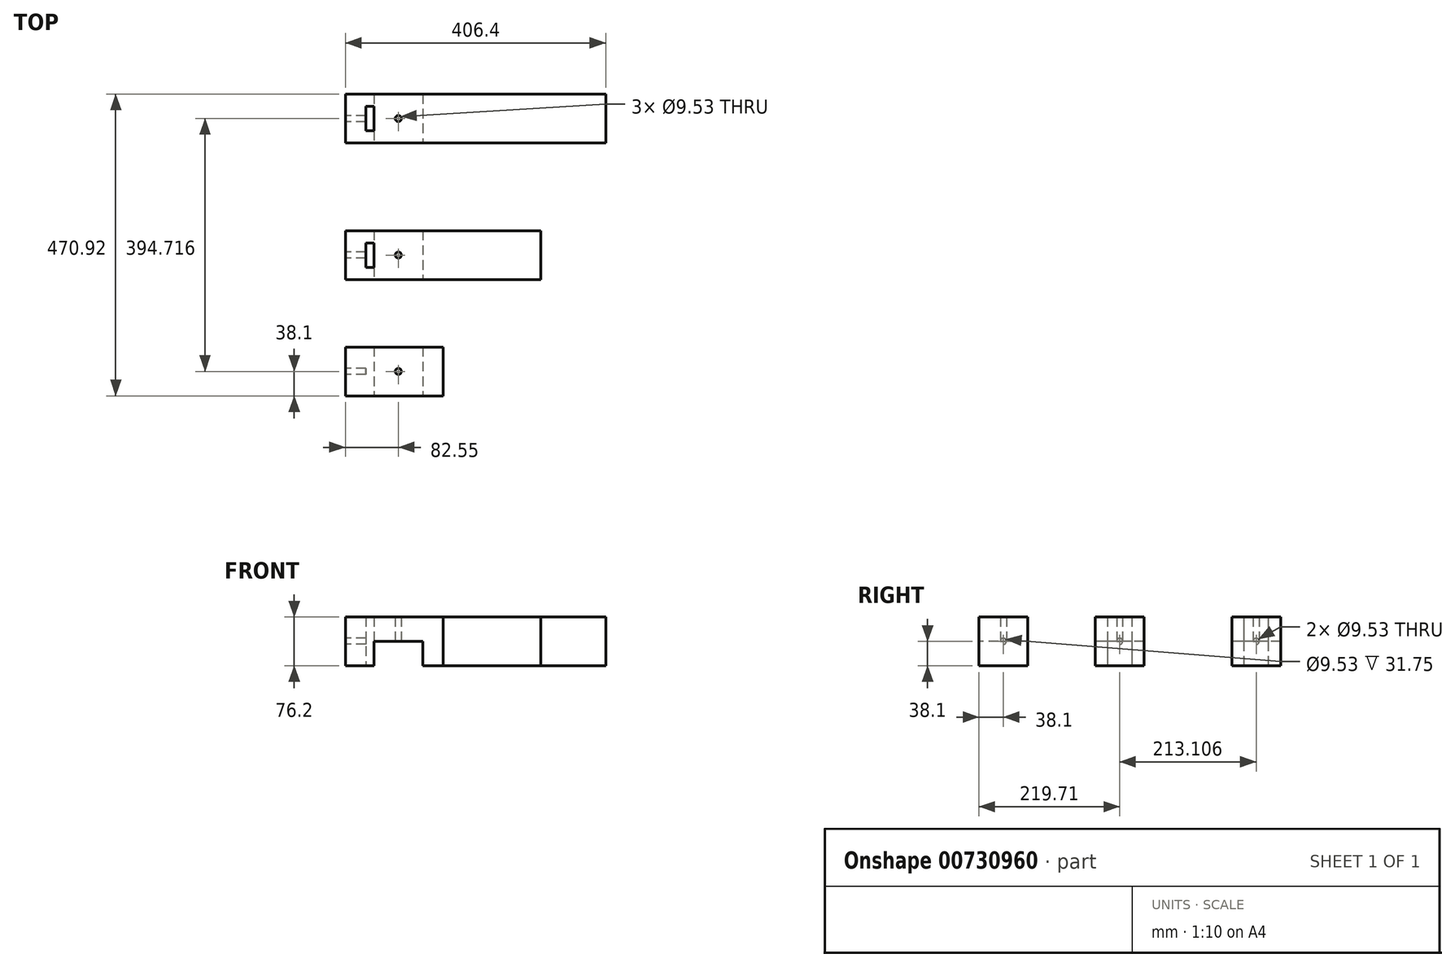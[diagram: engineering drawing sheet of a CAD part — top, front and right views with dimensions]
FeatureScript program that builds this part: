
annotation { "Feature Type Name" : "Feature", "Feature Type Description" : "" }
export const myFeature = defineFeature(function(context is Context, id is Id, definition is map)
    precondition{}
    {
        {
            var Q0;
            Q0=qCreatedBy(makeId("Right.planeOp"),FACE);
            var sketch = newSketch(context, id + "F0", { "sketchPlane" : qUnion([Q0])});
            skLineSegment(sketch, "E0.bottom", {"start": v(0, 0) * mm, "end": v(76.2, 0) * mm});
            skLineSegment(sketch, "E0.top", {"start": v(0, 76.2) * mm, "end": v(76.2, 76.2) * mm});
            skLineSegment(sketch, "E0.left", {"start": v(0, 0) * mm, "end": v(0, 76.2) * mm});
            skLineSegment(sketch, "E0.right", {"start": v(76.2, 0) * mm, "end": v(76.2, 76.2) * mm});
            skSolve(sketch);
        }
        {
            var Q0;
            Q0 = qSketchRegion(id + "F0", true);
            extrude(context, id + "F1", {"entities" : qUnion([Q0]), "depth" : 152.4 * mm, "offsetDistance" : 25.4 * mm});
        }
        {
            var Q0;
            Q0=makeQuery(id+"F1.opExtrude","SWEPT_FACE",FACE,{"disambiguationData":[OSD([sQuery(id+"F0.wireOp",EDGE,"E0.left")])]});
            var sketch = newSketch(context, id + "F2", { "sketchPlane" : qUnion([Q0])});
            skLineSegment(sketch, "E1.bottom", {"start": v(44.45, 0) * mm, "end": v(120.65, 0) * mm});
            skLineSegment(sketch, "E1.top", {"start": v(44.45, 38.1) * mm, "end": v(120.65, 38.1) * mm});
            skLineSegment(sketch, "E1.left", {"start": v(44.45, 0) * mm, "end": v(44.45, 38.1) * mm});
            skLineSegment(sketch, "E1.right", {"start": v(120.65, 0) * mm, "end": v(120.65, 38.1) * mm});
            skLineSegment(sketch, "E2", {"start": v(0, 0) * mm, "end": v(44.45, 0) * mm, "construction": true});
            skSolve(sketch);
        }
        {
            var Q0;
            Q0=makeQuery(id+"F2.imprint","IMPRINT",FACE,{"disambiguationData":[TD([[makeQuery(id+"F2.imprint","IMPRINT",EDGE,{"derivedFrom":sQuery(id+"F2.wireOp",EDGE,"E1.bottom")}),-1.0]])]});
            extrude(context, id + "F3", {"entities" : qUnion([Q0]), "operationType" : NewBodyOperationType.REMOVE, "oppositeDirection" : true, "depth" : 76.2 * mm, "offsetDistance" : 25.4 * mm});
        }
        {
            var Q0;
            Q0=makeQuery(id+"F1.opExtrude","CAP_FACE",FACE,{"disambiguationData":[OSD([sQuery(id+"F0.wireOp",EDGE,"E0.bottom"),sQuery(id+"F0.wireOp",EDGE,"E0.top"),sQuery(id+"F0.wireOp",EDGE,"E0.left"),sQuery(id+"F0.wireOp",EDGE,"E0.right")])],"isStart":true});
            var sketch = newSketch(context, id + "F4", { "sketchPlane" : qUnion([Q0])});
            skCircle(sketch, "E3", {"center": v(-38.1, 38.1) * mm, "radius": 4.76 * mm});
            skSolve(sketch);
        }
        {
            var Q0;
            Q0 = qSketchRegion(id + "F4", true);
            extrude(context, id + "F5", {"entities" : qUnion([Q0]), "operationType" : NewBodyOperationType.REMOVE, "oppositeDirection" : true, "depth" : 31.75 * mm, "offsetDistance" : 25.4 * mm});
        }
        {
            var Q0;
            Q0=makeQuery(id+"F3.boolean.opBoolean","COPY",FACE,{"derivedFrom":makeQuery(id+"F3.opExtrude","SWEPT_FACE",FACE,{"disambiguationData":[OSD([sQuery(id+"F2.wireOp",EDGE,"E1.top")])]})});
            var sketch = newSketch(context, id + "F6", { "sketchPlane" : qUnion([Q0])});
            skCircle(sketch, "E4", {"center": v(82.55, -38.1) * mm, "radius": 4.76 * mm});
            skSolve(sketch);
        }
        {
            var Q0;
            Q0 = qSketchRegion(id + "F6", true);
            extrude(context, id + "F7", {"entities" : qUnion([Q0]), "operationType" : NewBodyOperationType.REMOVE, "endBound" : BoundingType.THROUGH_ALL, "oppositeDirection" : true, "depth" : 25.4 * mm, "offsetDistance" : 25.4 * mm});
        }
        {
            var Q0;
            Q0=makeQuery(id+"F1.opExtrude","SWEPT_BODY",BODY,{"disambiguationData":[OSD([sQuery(id+"F0.wireOp",EDGE,"E0.bottom"),sQuery(id+"F0.wireOp",EDGE,"E0.top"),sQuery(id+"F0.wireOp",EDGE,"E0.left"),sQuery(id+"F0.wireOp",EDGE,"E0.right")])]});
            var Q1;
            Q1=makeQuery(id+"F1.opExtrude","CAP_EDGE",EDGE,{"disambiguationData":[OSD([sQuery(id+"F0.wireOp",EDGE,"E0.top")])],"isStart":true});
            transform(context, id + "F8", {"entities" : qUnion([Q0]), "transformType" : TransformType.TRANSLATION_DISTANCE, "transformDirection" : qUnion([Q1]), "distance" : 181.6 * mm, "makeCopy" : true});
        }
        {
            var Q0;
            Q0=makeQuery(id+"F8.opPattern","COPY",FACE,{"derivedFrom":makeQuery(id+"F1.opExtrude","CAP_FACE",FACE,{"disambiguationData":[OSD([sQuery(id+"F0.wireOp",EDGE,"E0.bottom"),sQuery(id+"F0.wireOp",EDGE,"E0.top"),sQuery(id+"F0.wireOp",EDGE,"E0.left"),sQuery(id+"F0.wireOp",EDGE,"E0.right")])],"isStart":false}),"instanceName":"1"});
            extrude(context, id + "F9", {"entities" : qUnion([Q0]), "operationType" : NewBodyOperationType.ADD, "depth" : 152.4 * mm, "offsetDistance" : 25.4 * mm});
        }
        {
            var Q0;
            {var subQ2=sQuery(id+"F0.wireOp",EDGE,"E0.bottom");Q0=makeQuery(id+"F8.opPattern","COPY",FACE,{"derivedFrom":makeQuery(id+"F3.boolean.opBoolean","SPLIT",FACE,{"disambiguationData":[TD([makeQuery(id+"F3.opExtrude","SWEPT_FACE",FACE,{"disambiguationData":[OSD([sQuery(id+"F2.wireOp",EDGE,"E1.left")])]})])],"derivedFrom":makeQuery(id+"F1.opExtrude","SWEPT_FACE",FACE,{"disambiguationData":[OSD([subQ2])]})}),"instanceName":"1"});}
            var sketch = newSketch(context, id + "F10", { "sketchPlane" : qUnion([Q0])});
            skLineSegment(sketch, "E5.bottom", {"start": v(44.45, -200.66) * mm, "end": v(31.75, -200.66) * mm});
            skLineSegment(sketch, "E5.top", {"start": v(44.45, -238.76) * mm, "end": v(31.75, -238.76) * mm});
            skLineSegment(sketch, "E5.left", {"start": v(44.45, -200.66) * mm, "end": v(44.45, -238.76) * mm});
            skLineSegment(sketch, "E5.right", {"start": v(31.75, -200.66) * mm, "end": v(31.75, -238.76) * mm});
            skPoint(sketch, "E5.middle", {"position": v(38.1, -219.7) * mm});
            skSolve(sketch);
        }
        {
            var Q0;
            Q0 = qSketchRegion(id + "F10", true);
            extrude(context, id + "F11", {"entities" : qUnion([Q0]), "operationType" : NewBodyOperationType.REMOVE, "endBound" : BoundingType.THROUGH_ALL, "oppositeDirection" : true, "depth" : 25.4 * mm, "offsetDistance" : 25.4 * mm});
        }
        {
            var Q0;
            Q0=makeQuery(id+"F1.opExtrude","SWEPT_BODY",BODY,{"disambiguationData":[OSD([sQuery(id+"F0.wireOp",EDGE,"E0.bottom"),sQuery(id+"F0.wireOp",EDGE,"E0.top"),sQuery(id+"F0.wireOp",EDGE,"E0.left"),sQuery(id+"F0.wireOp",EDGE,"E0.right")])]});
            var Q1;
            Q1=makeQuery(id+"F1.opExtrude","CAP_EDGE",EDGE,{"disambiguationData":[OSD([sQuery(id+"F0.wireOp",EDGE,"E0.top")])],"isStart":true});
            transform(context, id + "F12", {"entities" : qUnion([Q0]), "transformType" : TransformType.TRANSLATION_DISTANCE, "transformDirection" : qUnion([Q1]), "distance" : 394.72 * mm, "makeCopy" : true});
        }
        {
            var Q0;
            Q0=makeQuery(id+"F12.opPattern","COPY",FACE,{"derivedFrom":makeQuery(id+"F1.opExtrude","CAP_FACE",FACE,{"disambiguationData":[OSD([sQuery(id+"F0.wireOp",EDGE,"E0.bottom"),sQuery(id+"F0.wireOp",EDGE,"E0.top"),sQuery(id+"F0.wireOp",EDGE,"E0.left"),sQuery(id+"F0.wireOp",EDGE,"E0.right")])],"isStart":false}),"instanceName":"1"});
            extrude(context, id + "F13", {"entities" : qUnion([Q0]), "operationType" : NewBodyOperationType.ADD, "depth" : 254 * mm, "offsetDistance" : 25.4 * mm});
        }
        {
            var Q0;
            {var subQ0=sQuery(id+"F0.wireOp",EDGE,"E0.top");Q0=makeQuery(id+"F13.boolean.opBoolean","MERGE",FACE,{"derivedFrom":[makeQuery(id+"F12.opPattern","COPY",FACE,{"derivedFrom":makeQuery(id+"F1.opExtrude","SWEPT_FACE",FACE,{"disambiguationData":[OSD([subQ0])]}),"instanceName":"1"}),makeQuery(id+"F13.opExtrude","SWEPT_FACE",FACE,{"disambiguationData":[OSD([subQ0])]})]});}
            var sketch = newSketch(context, id + "F14", { "sketchPlane" : qUnion([Q0])});
            skLineSegment(sketch, "E6.bottom", {"start": v(31.75, 451.87) * mm, "end": v(44.45, 451.87) * mm});
            skLineSegment(sketch, "E6.top", {"start": v(31.75, 413.77) * mm, "end": v(44.45, 413.77) * mm});
            skLineSegment(sketch, "E6.left", {"start": v(31.75, 451.87) * mm, "end": v(31.75, 413.77) * mm});
            skLineSegment(sketch, "E6.right", {"start": v(44.45, 451.87) * mm, "end": v(44.45, 413.77) * mm});
            skPoint(sketch, "E6.middle", {"position": v(38.1, 432.82) * mm});
            skSolve(sketch);
        }
        {
            var Q0;
            Q0 = qSketchRegion(id + "F14", true);
            extrude(context, id + "F15", {"entities" : qUnion([Q0]), "operationType" : NewBodyOperationType.REMOVE, "endBound" : BoundingType.THROUGH_ALL, "oppositeDirection" : true, "depth" : 25.4 * mm, "offsetDistance" : 25.4 * mm});
        }
    });
